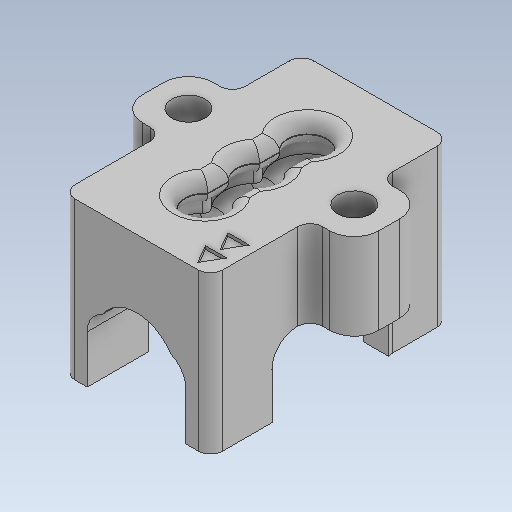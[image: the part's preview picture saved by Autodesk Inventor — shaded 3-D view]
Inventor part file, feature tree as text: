
AUTODESK INVENTOR PART (.ipt)
format: ipt  version: 2021 (Build 250183000, 183)  size: 672,256 bytes
history: native  units: mm
features: extrude x9, sketch x9, fillet x9, plane x1, emboss x1, projected_geometry x1
ambient origin geometry x8: Origin, YZ Plane, XZ Plane, XY Plane, X Axis, Y Axis, Z Axis, Center Point
bodies: Body1 (feature_tree)
feature tree (30):
  extrude  "Extrusion2"  Depth=19.4mm
  extrude  "Extrusion3"  Depth=7.0mm
  sketch  "Sketch11"  dims[d26=1.5mm d27=0.0mm d28=0.0mm]
  extrude  "Extrusion6"  TaperAngle=0.0deg  [1 undecoded]
  extrude  "Extrusion12"  TaperAngle=0.0deg  [1 undecoded]
  extrude  "Extrusion13"  Depth=6.0mm
  extrude  "Extrusion16"  Depth=7.137mm
  extrude  "Extrusion18"  Depth=6.0mm
  fillet  "Fillet4"  Radius=6.0mm
  plane  "Work Plane5"
  extrude  "Extrusion19"  Depth=2.0mm
  fillet  "Fillet7"  Radius=5.0mm
  fillet  "Fillet8"  Radius=2.0mm
  fillet  "Fillet9"  Radius=5.0mm
  fillet  "Fillet10"  Radius=2.0mm
  emboss  "Emboss4"
  fillet  "Fillet11"  Radius=5.0mm
  fillet  "Fillet12"  Radius=2.0mm
  fillet  "Fillet13"  Radius=5.0mm
  extrude  "Extrusion20"  Depth=1.0mm
  fillet  "Fillet14"  Radius=5.2mm
  sketch  "Sketch5"  dims[d6=12.0mm d7=19.4mm]
  sketch  "Sketch8"  dims[d8=7.0mm d9=0.0mm d25=6.6mm]
  sketch  "Sketch21"  dims[d43=7.0mm d44=0.0mm]
  sketch  "Sketch22"  dims[d109=0.0mm d110=0.0mm d111=6.0mm]
  sketch  "Sketch25"  dims[d112=6.0mm d116=7.137mm]
  sketch  "Sketch29"  dims[d117=1.75mm d118=6.0mm d119=6.0mm]
  sketch  "Sketch30"  dims[d120=3.5mm d121=0.0mm d131=2.0mm d132=5.0mm d133=2.0mm d134=5.0mm d135=2.0mm d136=5.0mm d137=2.0mm d138=5.0mm]
  sketch  "Sketch31"  dims[d139=5.74mm d140=0.0mm d177=5.5345mm d185=5.2mm d186=5.2mm d187=5.2mm d188=4.191mm d189=4.141mm d190=3.2mm d191=3.2mm d192=3.2mm d195=2.134mm d196=2.134mm d197=2.134mm d198=2.0mm d199=15.0mm d200=2.0mm d201=0.0mm d202=1.0mm d204=0.949mm d205=-5.1mm d206=3.3mm d207=3.3mm d208=3.3mm d209=2.2mm d210=15.0mm d212=2.0mm d213=0.0mm d216=0.949mm d217=0.949mm d218=1.0mm d220=0.5mm d221=0.25mm d222=0.0mm d223=2.0mm d224=0.6mm d225=0.25mm d226=2.7mm d227=0.734mm d228=8.455mm d229=5.7mm d230=5.7mm d231=0.0mm d232=0.0mm d233=2.0mm d234=1.0mm d235=1.5mm]
  projected_geometry  "Project Cut Edges4"
note: 2 required parameter values undecoded (feature->parameter linkage not recoverable at this tier; creation-order binding heuristic only, values carry confidence <= 0.55)
